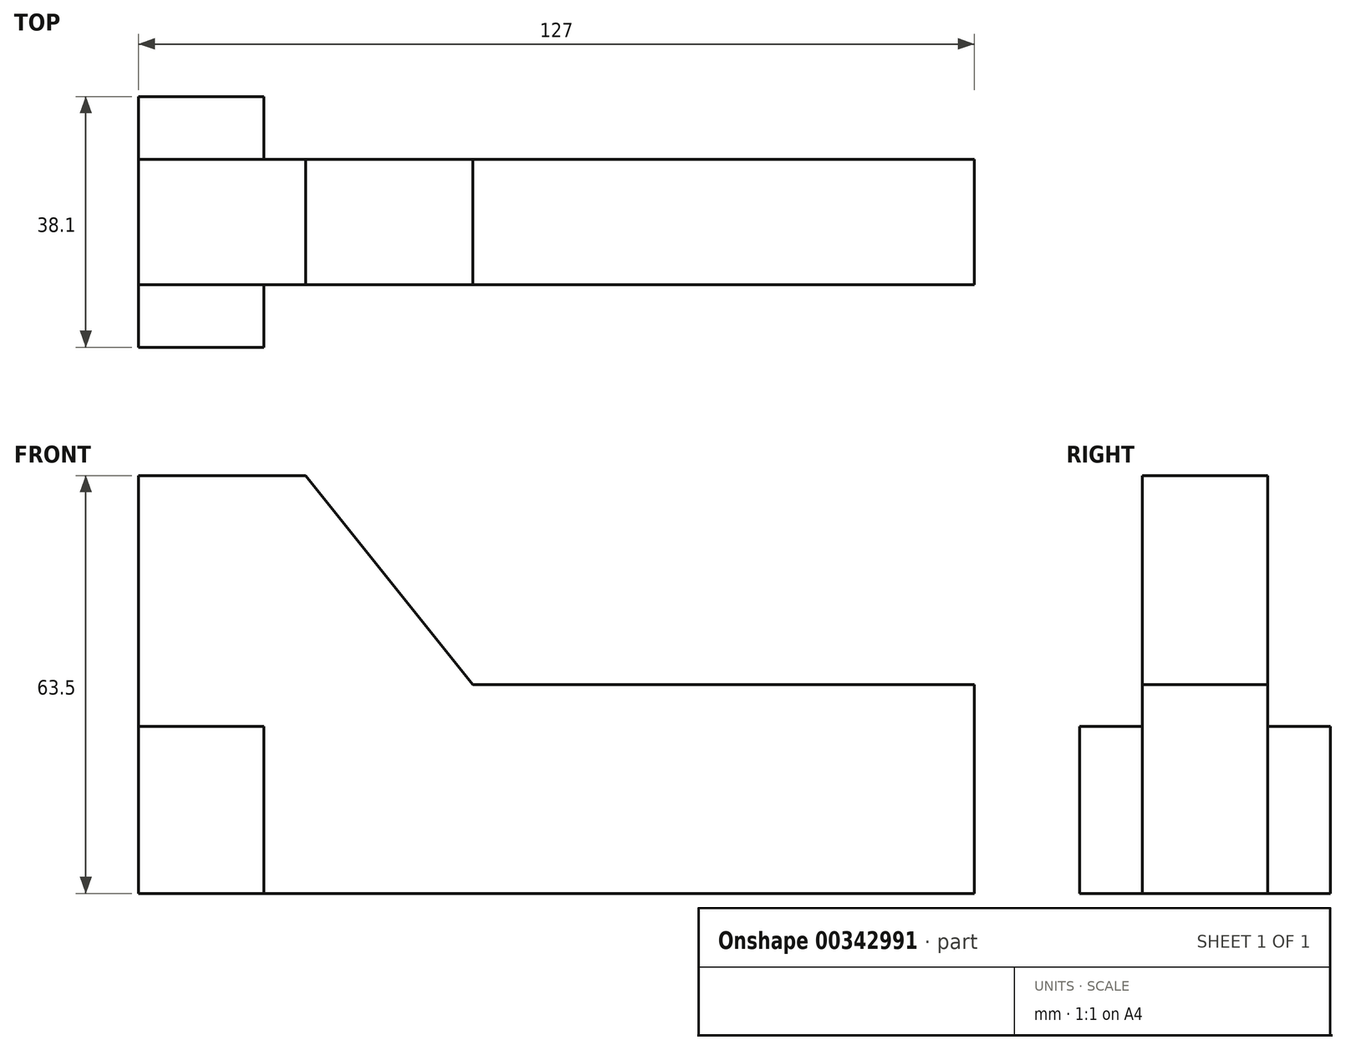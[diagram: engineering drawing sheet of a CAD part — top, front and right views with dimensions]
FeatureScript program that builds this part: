
annotation { "Feature Type Name" : "Feature", "Feature Type Description" : "" }
export const myFeature = defineFeature(function(context is Context, id is Id, definition is map)
    precondition{}
    {
        {
            var Q0;
            Q0=qCreatedBy(makeId("Front.planeOp"),FACE);
            var sketch = newSketch(context, id + "F0", { "sketchPlane" : qUnion([Q0])});
            skLineSegment(sketch, "E0", {"start": v(-71.37, -41.24) * mm, "end": v(55.63, -41.24) * mm});
            skLineSegment(sketch, "E1", {"start": v(-71.37, -41.24) * mm, "end": v(-71.37, 22.26) * mm});
            skLineSegment(sketch, "E2", {"start": v(55.63, -41.24) * mm, "end": v(55.63, -9.5) * mm});
            skLineSegment(sketch, "E3", {"start": v(55.63, -9.5) * mm, "end": v(-20.57, -9.5) * mm});
            skLineSegment(sketch, "E4", {"start": v(-71.37, 22.26) * mm, "end": v(-45.97, 22.26) * mm});
            skLineSegment(sketch, "E5", {"start": v(-45.97, 22.26) * mm, "end": v(-20.57, -9.5) * mm});
            skSolve(sketch);
        }
        {
            var Q0;
            Q0=makeQuery(id+"F0.imprint","IMPRINT",FACE,{"disambiguationData":[TD([[makeQuery(id+"F0.imprint","IMPRINT",EDGE,{"derivedFrom":sQuery(id+"F0.wireOp",EDGE,"E0")}),1.0]])]});
            extrude(context, id + "F1", {"entities" : qUnion([Q0]), "depth" : 19.05 * mm});
        }
        {
            var Q0;
            Q0=makeQuery(id+"F1.opExtrude","CAP_FACE",FACE,{"disambiguationData":[OSD([sQuery(id+"F0.wireOp",EDGE,"E0"),sQuery(id+"F0.wireOp",EDGE,"E1"),sQuery(id+"F0.wireOp",EDGE,"E2"),sQuery(id+"F0.wireOp",EDGE,"E3"),sQuery(id+"F0.wireOp",EDGE,"E4"),sQuery(id+"F0.wireOp",EDGE,"E5")])],"isStart":false});
            var sketch = newSketch(context, id + "F2", { "sketchPlane" : qUnion([Q0])});
            skLineSegment(sketch, "E6", {"start": v(-71.37, -41.24) * mm, "end": v(-71.37, -15.84) * mm});
            skLineSegment(sketch, "E7", {"start": v(-71.37, -41.24) * mm, "end": v(-52.32, -41.24) * mm});
            skLineSegment(sketch, "E8", {"start": v(-71.37, -15.84) * mm, "end": v(-52.32, -15.84) * mm});
            skLineSegment(sketch, "E9", {"start": v(-52.32, -15.84) * mm, "end": v(-52.32, -41.24) * mm});
            skSolve(sketch);
        }
        {
            var Q0;
            Q0=makeQuery(id+"F2.imprint","IMPRINT",FACE,{"disambiguationData":[TD([[makeQuery(id+"F2.imprint","IMPRINT",EDGE,{"derivedFrom":sQuery(id+"F2.wireOp",EDGE,"E6")}),-1.0]])]});
            extrude(context, id + "F3", {"entities" : qUnion([Q0]), "operationType" : NewBodyOperationType.ADD, "depth" : 9.52 * mm, "hasSecondDirection" : true, "secondDirectionOppositeDirection" : true, "secondDirectionDepth" : 28.57 * mm});
        }
    });
